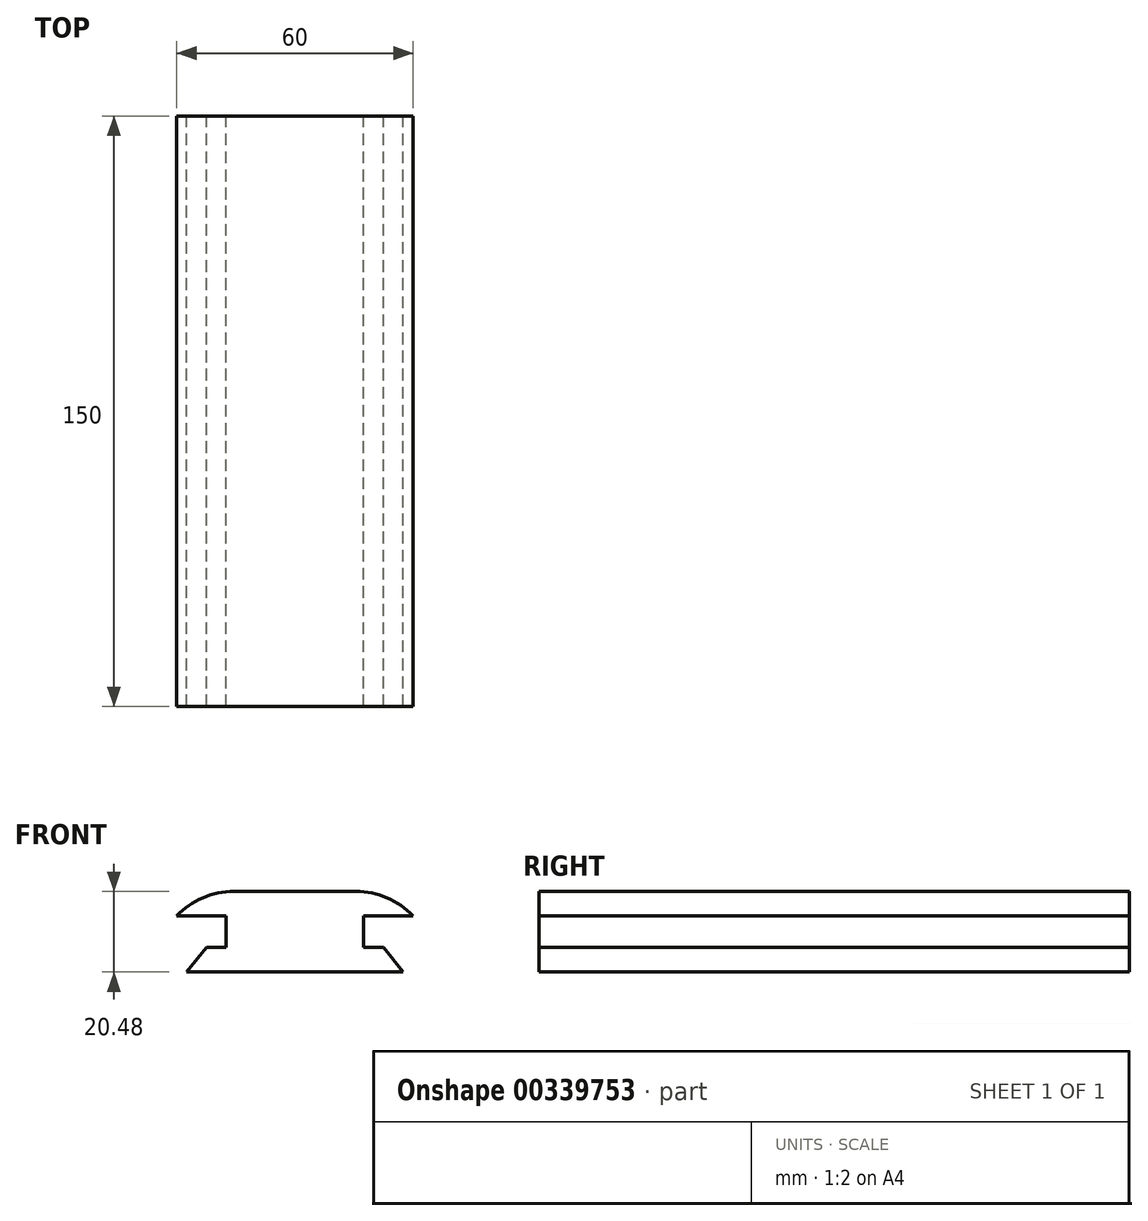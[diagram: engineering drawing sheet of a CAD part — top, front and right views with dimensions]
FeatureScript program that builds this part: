
annotation { "Feature Type Name" : "Feature", "Feature Type Description" : "" }
export const myFeature = defineFeature(function(context is Context, id is Id, definition is map)
    precondition{}
    {
        {
            var Q0;
            Q0=qCreatedBy(makeId("Front.planeOp"),FACE);
            var sketch = newSketch(context, id + "F0", { "sketchPlane" : qUnion([Q0])});
            skLineSegment(sketch, "E0.bottom", {"start": v(0, 0) * mm, "end": v(35, 0) * mm});
            skLineSegment(sketch, "E0.top", {"start": v(0, 8) * mm, "end": v(35, 8) * mm});
            skLineSegment(sketch, "E0.left", {"start": v(0, 0) * mm, "end": v(0, 8) * mm});
            skLineSegment(sketch, "E0.right", {"start": v(35, 0) * mm, "end": v(35, 8) * mm});
            skLineSegment(sketch, "E1", {"start": v(-12.5, 8) * mm, "end": v(47.5, 8) * mm});
            skPoint(sketch, "E1.endSnap0", {"position": v(17.5, 8) * mm});
            skLineSegment(sketch, "E2", {"start": v(47.5, 8) * mm, "end": v(42.5, 14.24) * mm});
            skLineSegment(sketch, "E3", {"start": v(42.5, 14.24) * mm, "end": v(-7.5, 14.24) * mm});
            skLineSegment(sketch, "E4", {"start": v(-7.5, 14.24) * mm, "end": v(-12.5, 8) * mm});
            skLineSegment(sketch, "E5", {"start": v(-5, 0) * mm, "end": v(40, 0) * mm});
            skLineSegment(sketch, "E6", {"start": v(40, 0) * mm, "end": v(45, -6.24) * mm});
            skLineSegment(sketch, "E7", {"start": v(45, -6.24) * mm, "end": v(-10, -6.24) * mm});
            skLineSegment(sketch, "E8", {"start": v(-10, -6.24) * mm, "end": v(-5, 0) * mm});
            skSolve(sketch);
        }
        {
            var Q0;
            Q0 = qSketchRegion(id + "F0", true);
            extrude(context, id + "F1", {"entities" : qUnion([Q0]), "depth" : 150 * mm});
        }
        {
            var Q0;
            Q0=makeQuery(id+"F1.opExtrude","SWEPT_EDGE",EDGE,{"disambiguationData":[OSD([sQuery(id+"F0.wireOp",EDGE,"E3"),sQuery(id+"F0.wireOp",EDGE,"E4")])]});
            var Q1;
            Q1=makeQuery(id+"F1.opExtrude","SWEPT_EDGE",EDGE,{"disambiguationData":[OSD([sQuery(id+"F0.wireOp",EDGE,"E2"),sQuery(id+"F0.wireOp",EDGE,"E3")])]});
            fillet(context, id + "F2", {"entities" : qUnion([Q0, Q1]), "radius" : 20 * mm, "tangentPropagation" : true, "allowEdgeOverflow" : false});
        }
    });
